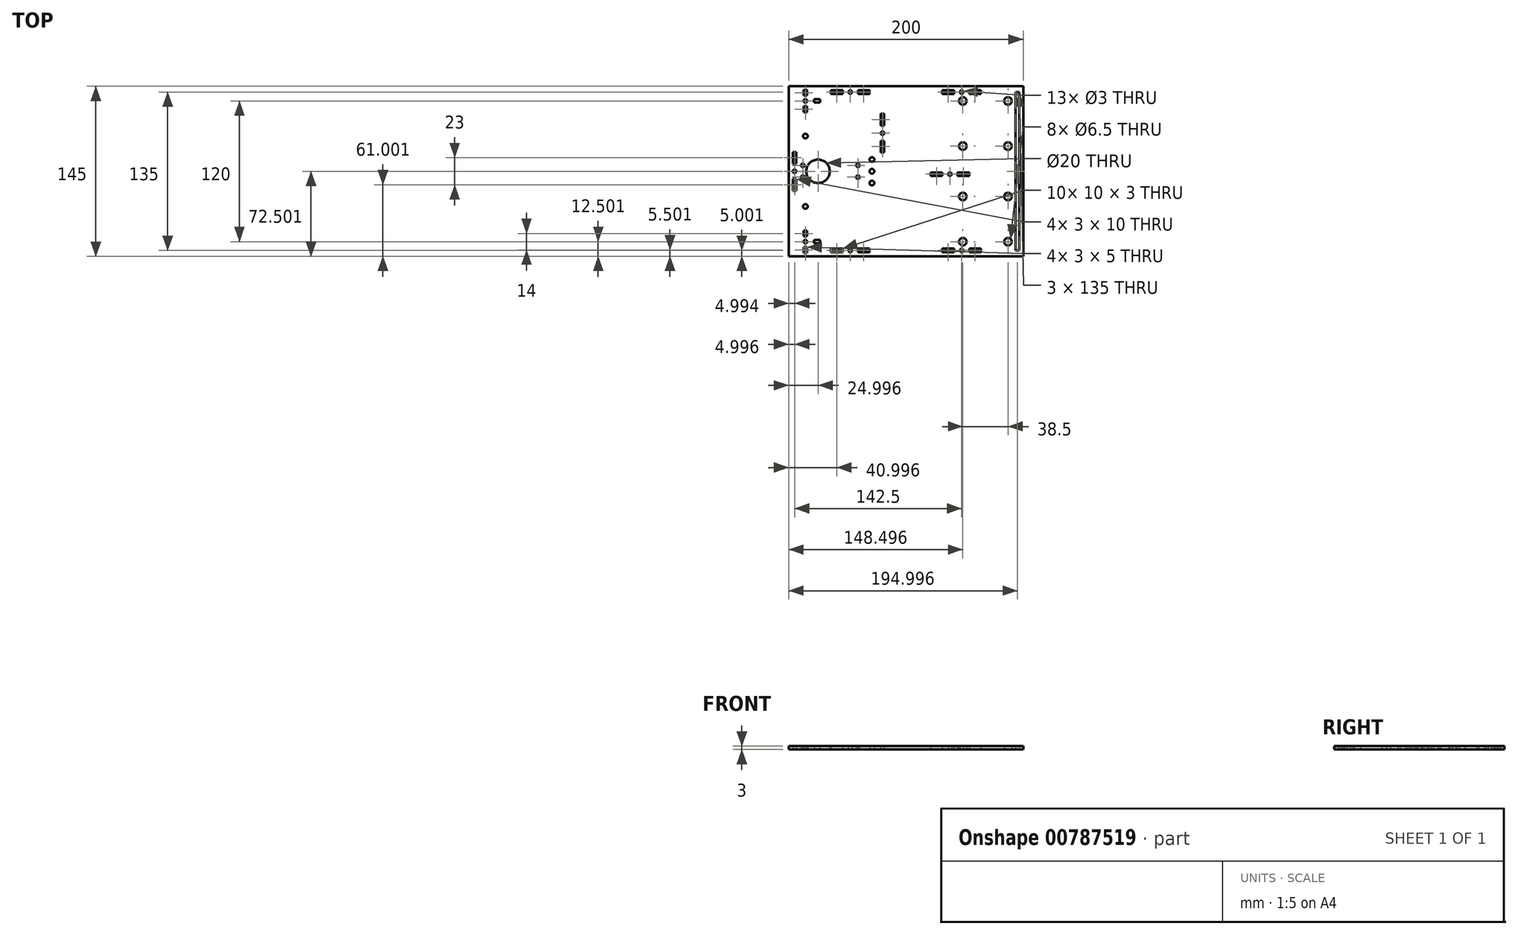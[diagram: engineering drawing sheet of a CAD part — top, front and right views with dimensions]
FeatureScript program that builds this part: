
annotation { "Feature Type Name" : "Feature", "Feature Type Description" : "" }
export const myFeature = defineFeature(function(context is Context, id is Id, definition is map)
    precondition{}
    {
        {
            var Q0;
            Q0=qCreatedBy(makeId("Top.planeOp"),FACE);
            var sketch = newSketch(context, id + "F0", { "sketchPlane" : qUnion([Q0])});
            skLineSegment(sketch, "E0.bottom", {"start": v(-93.6, 68.35) * mm, "end": v(106.4, 68.35) * mm});
            skLineSegment(sketch, "E0.top", {"start": v(-93.6, -76.65) * mm, "end": v(106.4, -76.65) * mm});
            skLineSegment(sketch, "E0.left", {"start": v(-93.6, 68.35) * mm, "end": v(-93.6, -76.65) * mm});
            skLineSegment(sketch, "E0.right", {"start": v(106.4, 68.35) * mm, "end": v(106.4, -76.65) * mm});
            skLineSegment(sketch, "E1.top", {"start": v(101.4, -6.65) * mm, "end": v(-13.6, -6.65) * mm, "construction": true});
            skLineSegment(sketch, "E1.right", {"start": v(-13.6, 63.35) * mm, "end": v(-13.6, -6.65) * mm, "construction": true});
            skLineSegment(sketch, "E2", {"start": v(-93.6, -4.15) * mm, "end": v(-78.6, -4.15) * mm, "construction": true});
            skLineSegment(sketch, "E3.0", {"start": v(101.4, 63.35) * mm, "end": v(101.4, -71.65) * mm, "construction": true});
            skLineSegment(sketch, "E4.bottom", {"start": v(99.9, 63.35) * mm, "end": v(102.9, 63.35) * mm});
            skLineSegment(sketch, "E4.top", {"start": v(99.9, -71.65) * mm, "end": v(102.9, -71.65) * mm});
            skLineSegment(sketch, "E4.left", {"start": v(99.9, 63.35) * mm, "end": v(99.9, -71.65) * mm});
            skLineSegment(sketch, "E4.right", {"start": v(102.9, 63.35) * mm, "end": v(102.9, -71.65) * mm});
            skPoint(sketch, "E4.middle", {"position": v(101.4, -4.15) * mm});
            skLineSegment(sketch, "E5.0", {"start": v(-88.6, 63.35) * mm, "end": v(109.77, 63.35) * mm, "construction": true});
            skLineSegment(sketch, "E6.0", {"start": v(-88.6, 63.35) * mm, "end": v(-88.6, -71.65) * mm, "construction": true});
            skLineSegment(sketch, "E7.0", {"start": v(-88.6, -71.65) * mm, "end": v(102.9, -71.65) * mm, "construction": true});
            skCircle(sketch, "E8", {"center": v(53.9, 63.35) * mm, "radius": 1.5 * mm});
            skCircle(sketch, "E9", {"center": v(-41.1, 63.35) * mm, "radius": 1.5 * mm});
            skPoint(sketch, "E10", {"position": v(-88.6, 63.35) * mm});
            skLineSegment(sketch, "E11.bottom", {"start": v(-57.6, 64.85) * mm, "end": v(-47.6, 64.85) * mm});
            skLineSegment(sketch, "E11.top", {"start": v(-57.6, 61.85) * mm, "end": v(-47.6, 61.85) * mm});
            skLineSegment(sketch, "E11.left", {"start": v(-57.6, 64.85) * mm, "end": v(-57.6, 61.85) * mm});
            skLineSegment(sketch, "E11.right", {"start": v(-47.6, 64.85) * mm, "end": v(-47.6, 61.85) * mm});
            skPoint(sketch, "E11.middle", {"position": v(-52.6, 63.35) * mm});
            skLineSegment(sketch, "E12.bottom", {"start": v(-34.6, 64.85) * mm, "end": v(-24.6, 64.85) * mm});
            skLineSegment(sketch, "E12.top", {"start": v(-34.6, 61.85) * mm, "end": v(-24.6, 61.85) * mm});
            skLineSegment(sketch, "E12.left", {"start": v(-34.6, 64.85) * mm, "end": v(-34.6, 61.85) * mm});
            skLineSegment(sketch, "E12.right", {"start": v(-24.6, 64.85) * mm, "end": v(-24.6, 61.85) * mm});
            skPoint(sketch, "E12.middle", {"position": v(-29.6, 63.35) * mm});
            skLineSegment(sketch, "E13.bottom", {"start": v(37.4, 64.85) * mm, "end": v(47.4, 64.85) * mm});
            skLineSegment(sketch, "E13.top", {"start": v(37.4, 61.85) * mm, "end": v(47.4, 61.85) * mm});
            skLineSegment(sketch, "E13.left", {"start": v(37.4, 64.85) * mm, "end": v(37.4, 61.85) * mm});
            skLineSegment(sketch, "E13.right", {"start": v(47.4, 64.85) * mm, "end": v(47.4, 61.85) * mm});
            skPoint(sketch, "E13.middle", {"position": v(42.4, 63.35) * mm});
            skLineSegment(sketch, "E14.bottom", {"start": v(60.4, 64.85) * mm, "end": v(70.4, 64.85) * mm});
            skLineSegment(sketch, "E14.top", {"start": v(60.4, 61.85) * mm, "end": v(70.4, 61.85) * mm});
            skLineSegment(sketch, "E14.left", {"start": v(60.4, 64.85) * mm, "end": v(60.4, 61.85) * mm});
            skLineSegment(sketch, "E14.right", {"start": v(70.4, 64.85) * mm, "end": v(70.4, 61.85) * mm});
            skPoint(sketch, "E14.middle", {"position": v(65.4, 63.35) * mm});
            skLineSegment(sketch, "E15.MirrorCS", {"start": v(-24.6, -73.15) * mm, "end": v(-24.6, -70.15) * mm});
            skLineSegment(sketch, "E16.MirrorCS", {"start": v(-57.6, -73.15) * mm, "end": v(-47.6, -73.15) * mm});
            skLineSegment(sketch, "E17.MirrorCS", {"start": v(-57.6, -70.15) * mm, "end": v(-47.6, -70.15) * mm});
            skLineSegment(sketch, "E18.MirrorCS", {"start": v(-34.6, -73.15) * mm, "end": v(-24.6, -73.15) * mm});
            skLineSegment(sketch, "E19.MirrorCS", {"start": v(-57.6, -73.15) * mm, "end": v(-57.6, -70.15) * mm});
            skLineSegment(sketch, "E20.MirrorCS", {"start": v(-34.6, -70.15) * mm, "end": v(-24.6, -70.15) * mm});
            skCircle(sketch, "E21.MirrorC", {"center": v(-41.1, -71.65) * mm, "radius": 1.5 * mm});
            skPoint(sketch, "E22.MirrorP", {"position": v(-52.6, -71.65) * mm});
            skLineSegment(sketch, "E23.MirrorCS", {"start": v(-47.6, -73.15) * mm, "end": v(-47.6, -70.15) * mm});
            skLineSegment(sketch, "E24.MirrorCS", {"start": v(-34.6, -73.15) * mm, "end": v(-34.6, -70.15) * mm});
            skPoint(sketch, "E25.MirrorP", {"position": v(-29.6, -71.65) * mm});
            skLineSegment(sketch, "E26.MirrorCS", {"start": v(70.4, -73.15) * mm, "end": v(70.4, -70.15) * mm});
            skLineSegment(sketch, "E27.MirrorCS", {"start": v(47.4, -73.15) * mm, "end": v(47.4, -70.15) * mm});
            skLineSegment(sketch, "E28.MirrorCS", {"start": v(60.4, -73.15) * mm, "end": v(60.4, -70.15) * mm});
            skLineSegment(sketch, "E29.MirrorCS", {"start": v(37.4, -73.15) * mm, "end": v(37.4, -70.15) * mm});
            skPoint(sketch, "E30.MirrorP", {"position": v(65.4, -71.65) * mm});
            skCircle(sketch, "E31.MirrorC", {"center": v(53.9, -71.65) * mm, "radius": 1.5 * mm});
            skLineSegment(sketch, "E32.MirrorCS", {"start": v(37.4, -70.15) * mm, "end": v(47.4, -70.15) * mm});
            skLineSegment(sketch, "E33.MirrorCS", {"start": v(60.4, -70.15) * mm, "end": v(70.4, -70.15) * mm});
            skPoint(sketch, "E34.MirrorP", {"position": v(42.4, -71.65) * mm});
            skLineSegment(sketch, "E35.MirrorCS", {"start": v(37.4, -73.15) * mm, "end": v(47.4, -73.15) * mm});
            skLineSegment(sketch, "E36.MirrorCS", {"start": v(60.4, -73.15) * mm, "end": v(70.4, -73.15) * mm});
            skLineSegment(sketch, "E37.0.1.0", {"start": v(-12.1, 44.85) * mm, "end": v(-12.1, 34.85) * mm});
            skLineSegment(sketch, "E37.0.1.1", {"start": v(-15.1, 44.85) * mm, "end": v(-12.1, 44.85) * mm});
            skLineSegment(sketch, "E37.0.1.2", {"start": v(-15.1, 44.85) * mm, "end": v(-15.1, 34.85) * mm});
            skLineSegment(sketch, "E37.0.1.3", {"start": v(-15.1, 34.85) * mm, "end": v(-12.1, 34.85) * mm});
            skCircle(sketch, "E37.0.1.4", {"center": v(-13.6, 28.35) * mm, "radius": 1.5 * mm});
            skLineSegment(sketch, "E37.0.1.5", {"start": v(-15.1, 21.85) * mm, "end": v(-12.1, 21.85) * mm});
            skLineSegment(sketch, "E37.0.1.6", {"start": v(-12.1, 21.85) * mm, "end": v(-12.1, 11.85) * mm});
            skLineSegment(sketch, "E37.0.1.7", {"start": v(-15.1, 11.85) * mm, "end": v(-12.1, 11.85) * mm});
            skLineSegment(sketch, "E37.0.1.8", {"start": v(-15.1, 21.85) * mm, "end": v(-15.1, 11.85) * mm});
            skLineSegment(sketch, "E37.0.2.0", {"start": v(27.4, -5.15) * mm, "end": v(37.4, -5.15) * mm});
            skLineSegment(sketch, "E37.0.2.1", {"start": v(27.4, -8.15) * mm, "end": v(27.4, -5.15) * mm});
            skLineSegment(sketch, "E37.0.2.2", {"start": v(27.4, -8.15) * mm, "end": v(37.4, -8.15) * mm});
            skLineSegment(sketch, "E37.0.2.3", {"start": v(37.4, -8.15) * mm, "end": v(37.4, -5.15) * mm});
            skCircle(sketch, "E37.0.2.4", {"center": v(43.9, -6.65) * mm, "radius": 1.5 * mm});
            skLineSegment(sketch, "E37.0.2.5", {"start": v(50.4, -8.15) * mm, "end": v(50.4, -5.15) * mm});
            skLineSegment(sketch, "E37.0.2.6", {"start": v(50.4, -5.15) * mm, "end": v(60.4, -5.15) * mm});
            skLineSegment(sketch, "E37.0.2.7", {"start": v(60.4, -8.15) * mm, "end": v(60.4, -5.15) * mm});
            skLineSegment(sketch, "E37.0.2.8", {"start": v(50.4, -8.15) * mm, "end": v(60.4, -8.15) * mm});
            skLineSegment(sketch, "E38.0.1.0", {"start": v(-87.1, 12.35) * mm, "end": v(-87.1, 2.35) * mm});
            skLineSegment(sketch, "E38.0.1.1", {"start": v(-90.1, 12.35) * mm, "end": v(-87.1, 12.35) * mm});
            skLineSegment(sketch, "E38.0.1.2", {"start": v(-90.1, 12.35) * mm, "end": v(-90.1, 2.35) * mm});
            skLineSegment(sketch, "E38.0.1.3", {"start": v(-90.1, 2.35) * mm, "end": v(-87.1, 2.35) * mm});
            skCircle(sketch, "E38.0.1.4", {"center": v(-88.6, -4.15) * mm, "radius": 1.5 * mm});
            skLineSegment(sketch, "E38.0.1.5", {"start": v(-90.1, -10.65) * mm, "end": v(-87.1, -10.65) * mm});
            skLineSegment(sketch, "E38.0.1.6", {"start": v(-87.1, -10.65) * mm, "end": v(-87.1, -20.65) * mm});
            skLineSegment(sketch, "E38.0.1.7", {"start": v(-90.1, -20.65) * mm, "end": v(-87.1, -20.65) * mm});
            skLineSegment(sketch, "E38.0.1.8", {"start": v(-90.1, -10.65) * mm, "end": v(-90.1, -20.65) * mm});
            skLineSegment(sketch, "E39.0", {"start": v(-34.6, -1.4) * mm, "end": v(-34.6, -21.9) * mm, "construction": true});
            skLineSegment(sketch, "E40.0", {"start": v(-81.6, -1.4) * mm, "end": v(-81.6, -21.9) * mm, "construction": true});
            skLineSegment(sketch, "E41.0", {"start": v(-93.6, -9.15) * mm, "end": v(-78.6, -9.15) * mm, "construction": true});
            skLineSegment(sketch, "E42.0", {"start": v(-93.6, 0.85) * mm, "end": v(-78.6, 0.85) * mm, "construction": true});
            skCircle(sketch, "E43", {"center": v(-81.6, 0.85) * mm, "radius": 1.5 * mm});
            skCircle(sketch, "E44", {"center": v(-81.6, -9.15) * mm, "radius": 1.5 * mm});
            skLineSegment(sketch, "E45", {"start": v(-37.6, -4.15) * mm, "end": v(-29.52, -4.15) * mm, "construction": true});
            skCircle(sketch, "E46", {"center": v(-34.6, 0.85) * mm, "radius": 1.5 * mm});
            skCircle(sketch, "E47", {"center": v(-34.6, -9.15) * mm, "radius": 1.5 * mm});
            skLineSegment(sketch, "E48", {"start": v(106.4, -4.15) * mm, "end": v(278.65, -4.15) * mm, "construction": true});
            skCircle(sketch, "E49", {"center": v(93.4, 55.85) * mm, "radius": 3.25 * mm});
            skCircle(sketch, "E50", {"center": v(54.9, 55.85) * mm, "radius": 3.25 * mm});
            skCircle(sketch, "E51", {"center": v(54.9, 17.35) * mm, "radius": 3.25 * mm});
            skCircle(sketch, "E52", {"center": v(93.4, 17.35) * mm, "radius": 3.25 * mm});
            skCircle(sketch, "E53.MirrorC", {"center": v(93.4, -64.15) * mm, "radius": 3.25 * mm});
            skCircle(sketch, "E54.MirrorC", {"center": v(93.4, -25.65) * mm, "radius": 3.25 * mm});
            skCircle(sketch, "E55.MirrorC", {"center": v(54.9, -25.65) * mm, "radius": 3.25 * mm});
            skCircle(sketch, "E56.MirrorC", {"center": v(54.9, -64.15) * mm, "radius": 3.25 * mm});
            skCircle(sketch, "E57", {"center": v(-68.6, -4.15) * mm, "radius": 10 * mm});
            skCircle(sketch, "E58", {"center": v(-79.34, 25.85) * mm, "radius": 2 * mm});
            skCircle(sketch, "E59", {"center": v(-22.6, -4.15) * mm, "radius": 2 * mm});
            skCircle(sketch, "E60", {"center": v(-22.6, 5.85) * mm, "radius": 2 * mm});
            skCircle(sketch, "E61", {"center": v(-22.6, -14.15) * mm, "radius": 2 * mm});
            skCircle(sketch, "E62.MirrorC", {"center": v(-79.34, -34.15) * mm, "radius": 2 * mm});
            skLineSegment(sketch, "E63", {"start": v(-79.34, 25.85) * mm, "end": v(-79.34, 83.4) * mm, "construction": true});
            skCircle(sketch, "E64", {"center": v(-79.34, 55.85) * mm, "radius": 1.5 * mm});
            skLineSegment(sketch, "E65.bottom", {"start": v(-80.84, 51.35) * mm, "end": v(-77.84, 51.35) * mm});
            skLineSegment(sketch, "E65.top", {"start": v(-80.84, 46.35) * mm, "end": v(-77.84, 46.35) * mm});
            skLineSegment(sketch, "E65.left", {"start": v(-80.84, 51.35) * mm, "end": v(-80.84, 46.35) * mm});
            skLineSegment(sketch, "E65.right", {"start": v(-77.84, 51.35) * mm, "end": v(-77.84, 46.35) * mm});
            skPoint(sketch, "E65.middle", {"position": v(-79.34, 48.85) * mm});
            skLineSegment(sketch, "E66.bottom", {"start": v(-80.84, 65.35) * mm, "end": v(-77.84, 65.35) * mm});
            skLineSegment(sketch, "E66.top", {"start": v(-80.84, 60.35) * mm, "end": v(-77.84, 60.35) * mm});
            skLineSegment(sketch, "E66.left", {"start": v(-80.84, 65.35) * mm, "end": v(-80.84, 60.35) * mm});
            skLineSegment(sketch, "E66.right", {"start": v(-77.84, 65.35) * mm, "end": v(-77.84, 60.35) * mm});
            skPoint(sketch, "E66.middle", {"position": v(-79.34, 62.85) * mm});
            skLineSegment(sketch, "E67.bottom", {"start": v(-71.84, 57.35) * mm, "end": v(-66.84, 57.35) * mm});
            skLineSegment(sketch, "E67.top", {"start": v(-71.84, 54.35) * mm, "end": v(-66.84, 54.35) * mm});
            skLineSegment(sketch, "E67.left", {"start": v(-71.84, 57.35) * mm, "end": v(-71.84, 54.35) * mm});
            skLineSegment(sketch, "E67.right", {"start": v(-66.84, 57.35) * mm, "end": v(-66.84, 54.35) * mm});
            skPoint(sketch, "E67.middle", {"position": v(-69.34, 55.85) * mm});
            skLineSegment(sketch, "E68", {"start": v(-79.34, -34.15) * mm, "end": v(-79.34, -118.61) * mm, "construction": true});
            skCircle(sketch, "E69", {"center": v(-79.34, -64.15) * mm, "radius": 1.5 * mm});
            skLineSegment(sketch, "E70.bottom", {"start": v(-80.84, -54.65) * mm, "end": v(-77.84, -54.65) * mm});
            skLineSegment(sketch, "E70.top", {"start": v(-80.84, -59.65) * mm, "end": v(-77.84, -59.65) * mm});
            skLineSegment(sketch, "E70.left", {"start": v(-80.84, -54.65) * mm, "end": v(-80.84, -59.65) * mm});
            skLineSegment(sketch, "E70.right", {"start": v(-77.84, -54.65) * mm, "end": v(-77.84, -59.65) * mm});
            skPoint(sketch, "E70.middle", {"position": v(-79.34, -57.15) * mm});
            skLineSegment(sketch, "E71.bottom", {"start": v(-80.84, -68.65) * mm, "end": v(-77.84, -68.65) * mm});
            skLineSegment(sketch, "E71.top", {"start": v(-80.84, -73.65) * mm, "end": v(-77.84, -73.65) * mm});
            skLineSegment(sketch, "E71.left", {"start": v(-80.84, -68.65) * mm, "end": v(-80.84, -73.65) * mm});
            skLineSegment(sketch, "E71.right", {"start": v(-77.84, -68.65) * mm, "end": v(-77.84, -73.65) * mm});
            skPoint(sketch, "E71.middle", {"position": v(-79.34, -71.15) * mm});
            skLineSegment(sketch, "E72.bottom", {"start": v(-71.84, -62.65) * mm, "end": v(-66.84, -62.65) * mm});
            skLineSegment(sketch, "E72.top", {"start": v(-71.84, -65.65) * mm, "end": v(-66.84, -65.65) * mm});
            skLineSegment(sketch, "E72.left", {"start": v(-71.84, -62.65) * mm, "end": v(-71.84, -65.65) * mm});
            skLineSegment(sketch, "E72.right", {"start": v(-66.84, -62.65) * mm, "end": v(-66.84, -65.65) * mm});
            skPoint(sketch, "E72.middle", {"position": v(-69.34, -64.15) * mm});
            skSolve(sketch);
        }
        {
            var Q0;
            Q0=makeQuery(id+"F0.imprint","IMPRINT",FACE,{"disambiguationData":[TD([[makeQuery(id+"F0.imprint","IMPRINT",EDGE,{"derivedFrom":sQuery(id+"F0.wireOp",EDGE,"E0.bottom")}),-1.0]])]});
            extrude(context, id + "F1", {"entities" : qUnion([Q0]), "depth" : 3 * mm, "offsetDistance" : 25.4 * mm});
        }
    });
